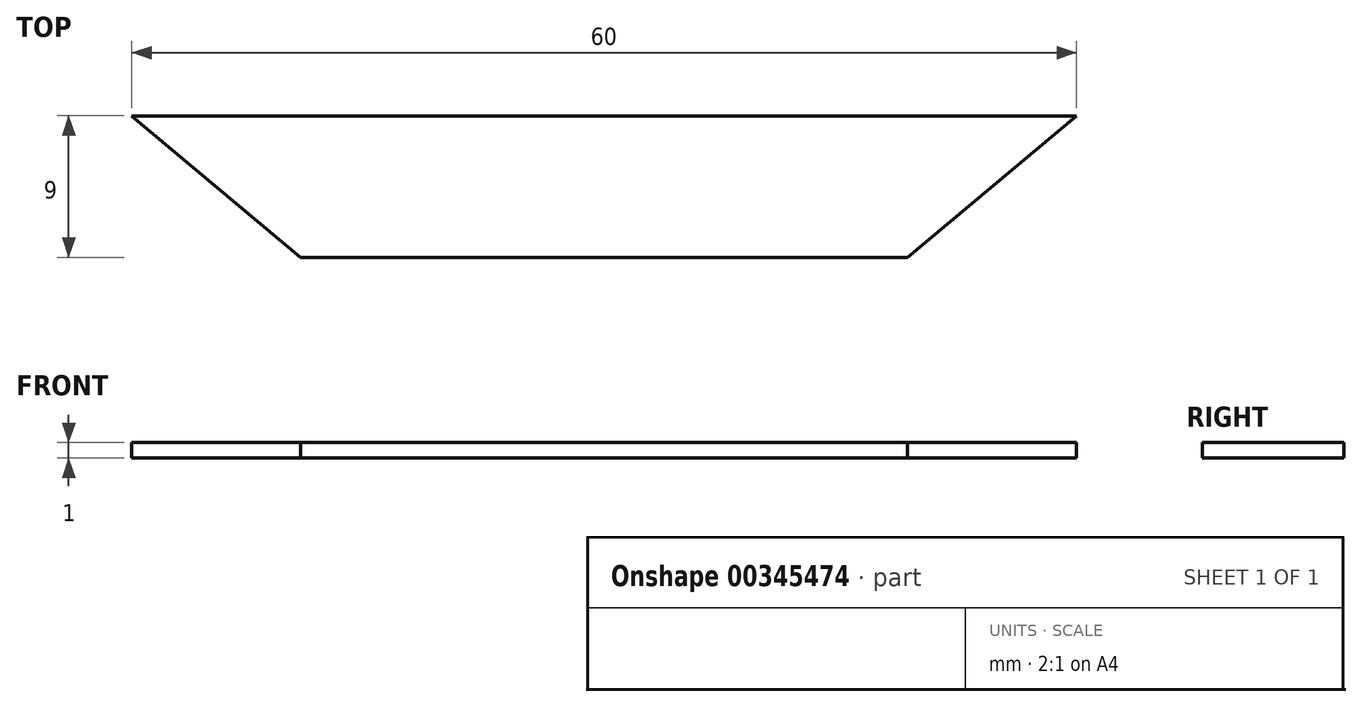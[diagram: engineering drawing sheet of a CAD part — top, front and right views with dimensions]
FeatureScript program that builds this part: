
annotation { "Feature Type Name" : "Feature", "Feature Type Description" : "" }
export const myFeature = defineFeature(function(context is Context, id is Id, definition is map)
    precondition{}
    {
        {
            var Q0;
            Q0=qCreatedBy(makeId("Top.planeOp"),FACE);
            var sketch = newSketch(context, id + "F0", { "sketchPlane" : qUnion([Q0])});
            skLineSegment(sketch, "E0.bottom", {"start": v(-6.23, 10.4) * mm, "end": v(53.77, 10.4) * mm});
            skLineSegment(sketch, "E0.top", {"start": v(4.5, 1.4) * mm, "end": v(43.04, 1.4) * mm});
            skLineSegment(sketch, "E1", {"start": v(-6.23, 10.4) * mm, "end": v(4.5, 1.4) * mm});
            skLineSegment(sketch, "E2", {"start": v(43.04, 1.4) * mm, "end": v(53.77, 10.4) * mm});
            skSolve(sketch);
        }
        {
            var Q0;
            Q0=makeQuery(id+"F0.imprint","IMPRINT",FACE,{"disambiguationData":[TD([[makeQuery(id+"F0.imprint","IMPRINT",EDGE,{"derivedFrom":sQuery(id+"F0.wireOp",EDGE,"E0.bottom")}),-1.0]])]});
            extrude(context, id + "F1", {"entities" : qUnion([Q0]), "depth" : 1 * mm});
        }
    });
